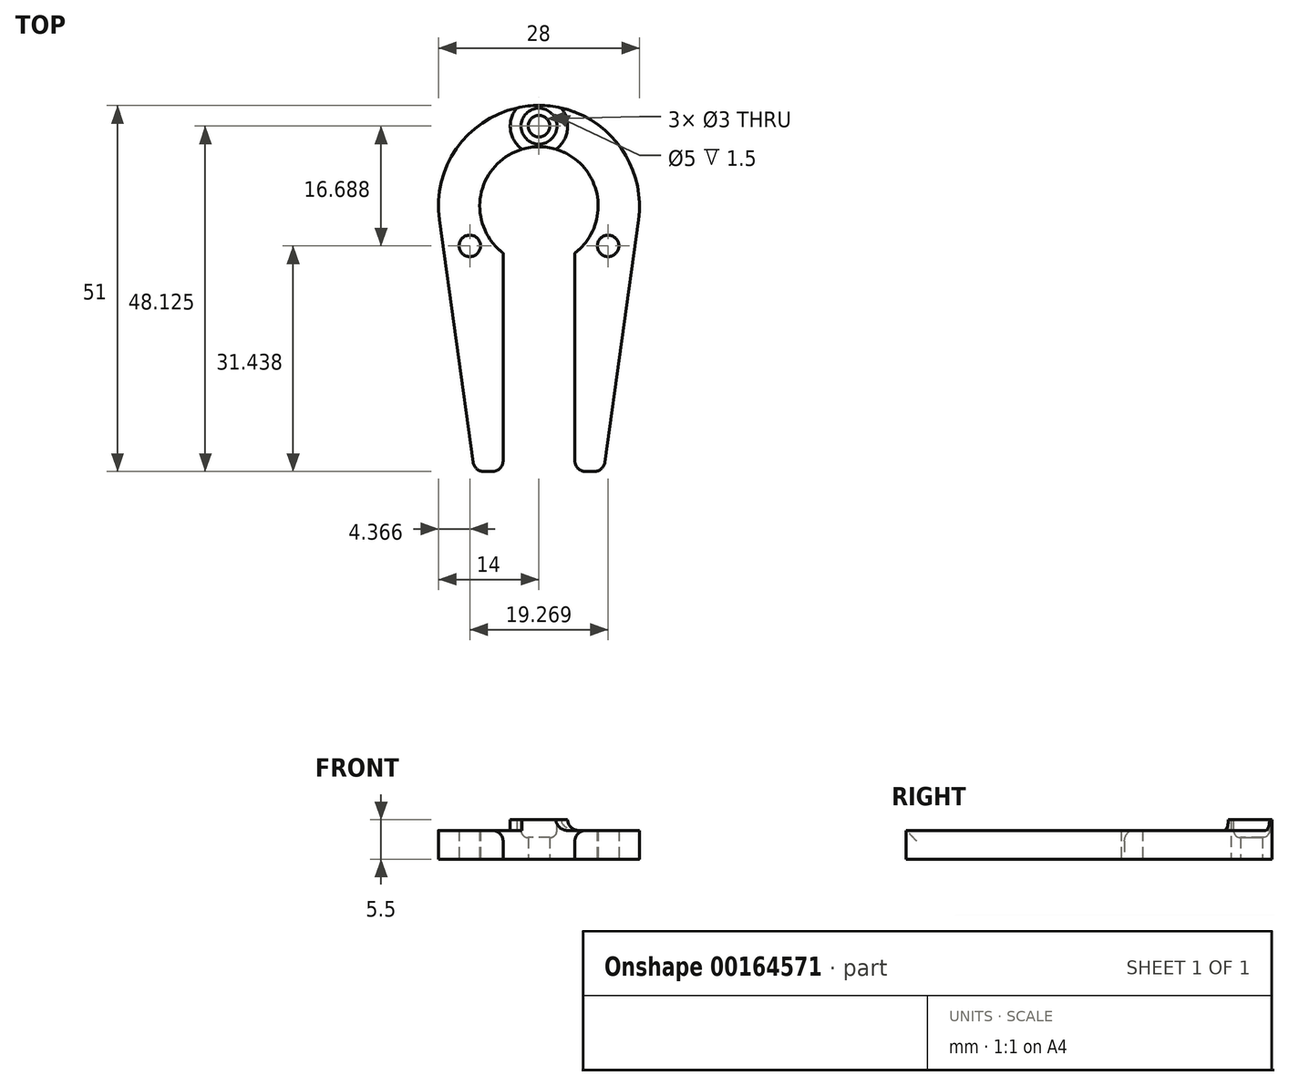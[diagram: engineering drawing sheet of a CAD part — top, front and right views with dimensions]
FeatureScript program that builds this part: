
annotation { "Feature Type Name" : "Feature", "Feature Type Description" : "" }
export const myFeature = defineFeature(function(context is Context, id is Id, definition is map)
    precondition{}
    {
        {
            var Q0;
            Q0=qCreatedBy(makeId("Top.planeOp"),FACE);
            var sketch = newSketch(context, id + "F0", { "sketchPlane" : qUnion([Q0])});
            skCircle(sketch, "E0", {"center": v(0, 0) * mm, "radius": 8.25 * mm});
            skCircle(sketch, "E1", {"center": v(0, 0) * mm, "radius": 14 * mm});
            skLineSegment(sketch, "E2", {"start": v(0, 14) * mm, "end": v(0, 8.25) * mm, "construction": true});
            skCircle(sketch, "E3", {"center": v(0, 11.12) * mm, "radius": 1.5 * mm});
            skCircle(sketch, "E4.1.0", {"center": v(-9.63, -5.56) * mm, "radius": 1.5 * mm});
            skCircle(sketch, "E4.2.0", {"center": v(9.63, -5.56) * mm, "radius": 1.5 * mm});
            skLineSegment(sketch, "E5.bottom", {"start": v(-5, -5) * mm, "end": v(5, -5) * mm});
            skLineSegment(sketch, "E5.top", {"start": v(-5, -37) * mm, "end": v(5, -37) * mm});
            skLineSegment(sketch, "E5.left", {"start": v(-5, -5) * mm, "end": v(-5, -37) * mm});
            skLineSegment(sketch, "E5.right", {"start": v(5, -5) * mm, "end": v(5, -37) * mm});
            skPoint(sketch, "E6", {"position": v(0, -5) * mm});
            skLineSegment(sketch, "E7", {"start": v(5, -37) * mm, "end": v(9, -37) * mm});
            skLineSegment(sketch, "E8", {"start": v(-5, -37) * mm, "end": v(-9, -37) * mm});
            skLineSegment(sketch, "E9", {"start": v(9, -37) * mm, "end": v(13.87, -1.92) * mm});
            skLineSegment(sketch, "E10", {"start": v(-9, -37) * mm, "end": v(-13.87, -1.92) * mm});
            skSolve(sketch);
        }
        {
            var Q0;
            Q0=makeQuery(id+"F0.imprint","IMPRINT",FACE,{"disambiguationData":[TD([[makeQuery(id+"F0.imprint","IMPRINT",EDGE,{"derivedFrom":sQuery(id+"F0.wireOp",EDGE,"E3")}),-1.0]])]});
            var Q1;
            {var subQ4=sQuery(id+"F0.wireOp",EDGE,"E8");Q1=makeQuery(id+"F0.imprint","IMPRINT",FACE,{"disambiguationData":[TD([[makeQuery(id+"F0.imprint","IMPRINT",EDGE,{"derivedFrom":subQ4}),-1.0]])]});}
            var Q2;
            {var subQ4=sQuery(id+"F0.wireOp",EDGE,"E7");Q2=makeQuery(id+"F0.imprint","IMPRINT",FACE,{"disambiguationData":[TD([[makeQuery(id+"F0.imprint","IMPRINT",EDGE,{"derivedFrom":subQ4}),1.0]])]});}
            extrude(context, id + "F1", {"entities" : qUnion([Q0, Q1, Q2]), "depth" : 4 * mm});
        }
        {
            var Q0;
            Q0=makeQuery(id+"F1.opExtrude","CAP_FACE",FACE,{"disambiguationData":[OSD([sQuery(id+"F0.wireOp",EDGE,"E0"),sQuery(id+"F0.wireOp",EDGE,"E1"),sQuery(id+"F0.wireOp",EDGE,"E3"),sQuery(id+"F0.wireOp",EDGE,"E4.1.0"),sQuery(id+"F0.wireOp",EDGE,"E4.2.0"),sQuery(id+"F0.wireOp",EDGE,"E5.left"),sQuery(id+"F0.wireOp",EDGE,"E5.right"),sQuery(id+"F0.wireOp",EDGE,"E7"),sQuery(id+"F0.wireOp",EDGE,"E8"),sQuery(id+"F0.wireOp",EDGE,"E9"),sQuery(id+"F0.wireOp",EDGE,"E10")])],"isStart":false});
            var sketch = newSketch(context, id + "F2", { "sketchPlane" : qUnion([Q0])});
            skCircle(sketch, "E11.0", {"center": v(0, 11.12) * mm, "radius": 1.5 * mm});
            skArc(sketch, "E11.1", {"start": v(13.87, -1.92) * mm, "mid": v(0, 14) * mm, "end": v(-13.87, -1.92) * mm});
            skArc(sketch, "E11.2", {"start": v(5, -6.56) * mm, "mid": v(0, 8.25) * mm, "end": v(-5, -6.56) * mm});
            skCircle(sketch, "E12", {"center": v(0, 11.12) * mm, "radius": 2.5 * mm});
            skCircle(sketch, "E13", {"center": v(0, 11.12) * mm, "radius": 4 * mm});
            skSolve(sketch);
        }
        {
            var Q0;
            Q0=makeQuery(id+"F2.imprint","IMPRINT",FACE,{"disambiguationData":[TD([[makeQuery(id+"F2.imprint","IMPRINT",EDGE,{"derivedFrom":sQuery(id+"F2.wireOp",EDGE,"E12")}),-1.0]])]});
            var Q1;
            Q1=makeQuery(id+"F2.imprint","IMPRINT",FACE,{"disambiguationData":[TD([[makeQuery(id+"F2.imprint","IMPRINT",EDGE,{"derivedFrom":sQuery(id+"F2.wireOp",EDGE,"E11.0")}),-1.0]])]});
            var Q2;
            Q2=makeQuery(id+"F2.imprint","IMPRINT",FACE,{"disambiguationData":[TD([[makeQuery(id+"F2.imprint","IMPRINT",EDGE,{"derivedFrom":sQuery(id+"F2.wireOp",EDGE,"E11.0")}),1.0]])]});
            extrude(context, id + "F3", {"entities" : qUnion([Q0, Q1, Q2]), "operationType" : NewBodyOperationType.ADD, "depth" : 1.5 * mm});
        }
        {
            var Q0;
            Q0=makeQuery(id+"F3.opExtrude","CAP_FACE",FACE,{"disambiguationData":[OSD([sQuery(id+"F2.wireOp",EDGE,"E11.1"),sQuery(id+"F2.wireOp",EDGE,"E11.2"),sQuery(id+"F2.wireOp",EDGE,"E13")])],"isStart":false});
            var sketch = newSketch(context, id + "F4", { "sketchPlane" : qUnion([Q0])});
            skCircle(sketch, "E14.0", {"center": v(0, 11.12) * mm, "radius": 2.5 * mm});
            skSolve(sketch);
        }
        {
            var Q0;
            Q0 = qSketchRegion(id + "F4", true);
            extrude(context, id + "F5", {"entities" : qUnion([Q0]), "operationType" : NewBodyOperationType.REMOVE, "oppositeDirection" : true, "depth" : 2.5 * mm});
        }
        {
            var Q0;
            Q0=makeQuery(id+"F5.boolean.opBoolean","COPY",EDGE,{"derivedFrom":makeQuery(id+"F5.opExtrude","CAP_EDGE",EDGE,{"disambiguationData":[OSD([sQuery(id+"F4.wireOp",EDGE,"E14.0")])],"isStart":false})});
            fillet(context, id + "F6", {"entities" : qUnion([Q0]), "radius" : 1 * mm, "tangentPropagation" : true, "allowEdgeOverflow" : false});
        }
        {
            var Q0;
            {var subQ0=sQuery(id+"F2.wireOp",EDGE,"E13");Q0=makeQuery(id+"F3.opExtrude","CAP_EDGE",EDGE,{"disambiguationData":[OSD([subQ0]),TDD([makeQuery(id+"F2.imprint","IMPRINT",EDGE,{"disambiguationData":[TD([[makeQuery(id+"F2.imprint","INTERSECT",VERTEX,{"disambiguationData":[OD(1.0)],"derivedFrom":[sQuery(id+"F2.wireOp",EDGE,"E11.1"),subQ0]}),-1.0]])],"derivedFrom":subQ0})])],"isStart":true});}
            var Q1;
            {var subQ0=sQuery(id+"F2.wireOp",EDGE,"E13");Q1=makeQuery(id+"F3.opExtrude","CAP_EDGE",EDGE,{"disambiguationData":[OSD([subQ0]),TDD([makeQuery(id+"F2.imprint","IMPRINT",EDGE,{"disambiguationData":[TD([[makeQuery(id+"F2.imprint","INTERSECT",VERTEX,{"disambiguationData":[OD(0.0)],"derivedFrom":[sQuery(id+"F2.wireOp",EDGE,"E11.1"),subQ0]}),1.0]])],"derivedFrom":subQ0})])],"isStart":true});}
            var Q2;
            Q2=makeQuery(id+"F1.opExtrude","CAP_EDGE",EDGE,{"disambiguationData":[OSD([sQuery(id+"F0.wireOp",EDGE,"E5.right")])],"isStart":false});
            var Q3;
            Q3=makeQuery(id+"F1.opExtrude","CAP_EDGE",EDGE,{"disambiguationData":[OSD([sQuery(id+"F0.wireOp",EDGE,"E5.left")])],"isStart":false});
            var Q4;
            Q4=makeQuery(id+"F1.opExtrude","SWEPT_EDGE",EDGE,{"disambiguationData":[OSD([sQuery(id+"F0.wireOp",EDGE,"E8"),sQuery(id+"F0.wireOp",EDGE,"E10")])]});
            var Q5;
            Q5=makeQuery(id+"F1.opExtrude","SWEPT_EDGE",EDGE,{"disambiguationData":[OSD([sQuery(id+"F0.wireOp",EDGE,"E7"),sQuery(id+"F0.wireOp",EDGE,"E9")])]});
            var Q6;
            Q6=makeQuery(id+"F1.opExtrude","SWEPT_EDGE",EDGE,{"disambiguationData":[OSD([sQuery(id+"F0.wireOp",EDGE,"E5.top"),sQuery(id+"F0.wireOp",EDGE,"E5.right"),sQuery(id+"F0.wireOp",EDGE,"E7")])]});
            var Q7;
            Q7=makeQuery(id+"F1.opExtrude","SWEPT_EDGE",EDGE,{"disambiguationData":[OSD([sQuery(id+"F0.wireOp",EDGE,"E5.top"),sQuery(id+"F0.wireOp",EDGE,"E5.left"),sQuery(id+"F0.wireOp",EDGE,"E8")])]});
            fillet(context, id + "F7", {"entities" : qUnion([Q0, Q1, Q2, Q3, Q4, Q5, Q6, Q7]), "radius" : 1.5 * mm, "tangentPropagation" : true, "allowEdgeOverflow" : false});
        }
    });
